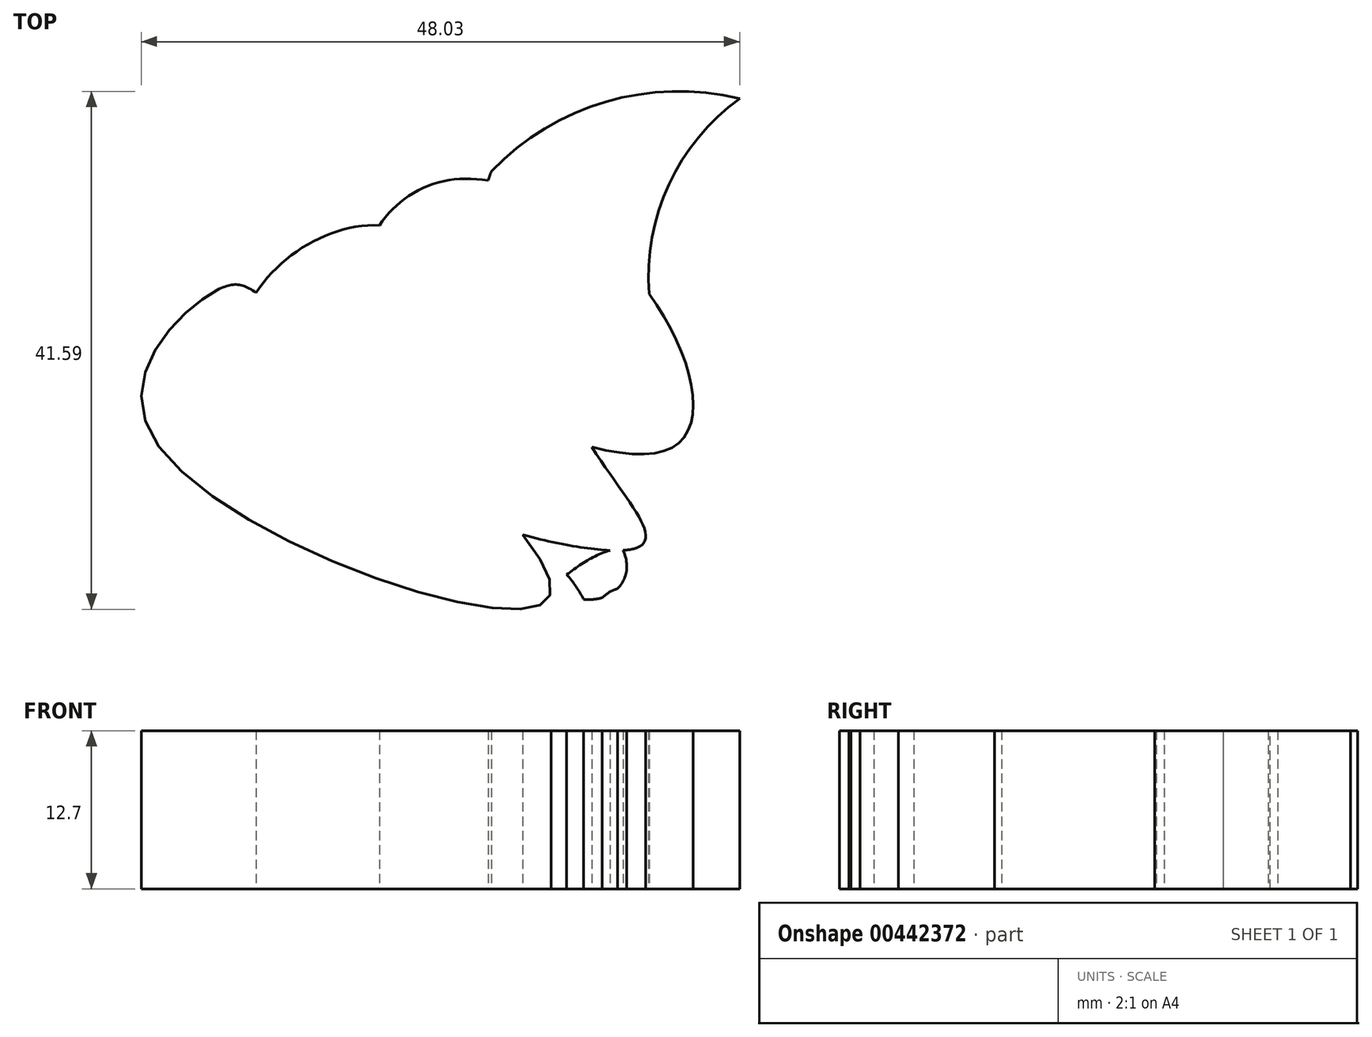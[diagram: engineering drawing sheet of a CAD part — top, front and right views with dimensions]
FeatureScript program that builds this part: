
annotation { "Feature Type Name" : "Feature", "Feature Type Description" : "" }
export const myFeature = defineFeature(function(context is Context, id is Id, definition is map)
    precondition{}
    {
        {
            var Q0;
            Q0=qCreatedBy(makeId("Top.planeOp"),FACE);
            var sketch = newSketch(context, id + "F0", { "sketchPlane" : qUnion([Q0])});
            skArc(sketch, "E0", {"start": v(-28.4, 40.22) * mm, "mid": v(-34.47, 32.4) * mm, "end": v(-35.4, 22.54) * mm});
            skArc(sketch, "E1", {"start": v(-28.4, 40.22) * mm, "mid": v(-39.13, 39.95) * mm, "end": v(-48.3, 34.38) * mm});
            skArc(sketch, "E2", {"start": v(-48.3, 34.38) * mm, "mid": v(-46, 23.94) * mm, "end": v(-35.4, 22.54) * mm});
            skSolve(sketch);
        }
        {
            var Q0;
            Q0=qCreatedBy(makeId("Top.planeOp"),FACE);
            var sketch = newSketch(context, id + "F1", { "sketchPlane" : qUnion([Q0])});
            skFitSpline(sketch, "E3", {"points": [v(-57.41, 30.02) * mm, v(-39.74, 11.43) * mm, v(-36.69, 4.11) * mm, v(-68.08, 18.14) * mm, v(-57.41, 30.02) * mm]});
            skFitSpline(sketch, "E4", {"points": [v(-43.25, 16.92) * mm, v(-36.69, 12.65) * mm, v(-36.69, 4.11) * mm, v(-43.25, 16.92) * mm]});
            skSolve(sketch);
        }
        {
            var Q0;
            Q0=qCreatedBy(makeId("Top.planeOp"),FACE);
            var sketch = newSketch(context, id + "F2", { "sketchPlane" : qUnion([Q0])});
            skPoint(sketch, "E5.3.internal.orphan", {"position": v(-41, 0) * mm});
            skFitSpline(sketch, "E6", {"points": [v(-65.13, 23.01) * mm, v(-70.3, 24.84) * mm, v(-75.8, 13.56) * mm, v(-43.8, 0) * mm, v(-65.13, 23.01) * mm]});
            skFitSpline(sketch, "E7", {"points": [v(-68.7, 19.35) * mm, v(-70.3, 24.84) * mm, v(-62.6, 24.84) * mm, v(-68.7, 19.35) * mm]});
            skSolve(sketch);
        }
        {
            var Q0;
            Q0=qCreatedBy(makeId("Top.planeOp"),FACE);
            var sketch = newSketch(context, id + "F3", { "sketchPlane" : qUnion([Q0])});
            skFitSpline(sketch, "E8", {"points": [v(-40.92, 0) * mm, v(-50.96, 9.3) * mm, v(-37.86, 4.11) * mm, v(-40.92, 0) * mm]});
            skFitSpline(sketch, "E9.trimOffspring", {"points": [v(-59.23, 0) * mm, v(-41.86, -7.47) * mm, v(-44.6, 3.81) * mm, v(-59.23, 0) * mm]});
            skPoint(sketch, "E10.0.internal.orphan", {"position": v(-57.45, 0) * mm});
            skFitSpline(sketch, "E11", {"points": [v(-41.86, -7.47) * mm, v(-34.97, -3.83) * mm, v(-38.2, 0.85) * mm, v(-41.86, -7.47) * mm]});
            skFitSpline(sketch, "E12", {"points": [v(-37.86, 4.11) * mm, v(-34.97, 0) * mm, v(-45.93, -3.83) * mm, v(-37.86, 4.11) * mm]});
            skSolve(sketch);
        }
        {
            var Q0;
            Q0=qCreatedBy(makeId("Top.planeOp"),FACE);
            var sketch = newSketch(context, id + "F4", { "sketchPlane" : qUnion([Q0])});
            skFitSpline(sketch, "E13", {"points": [v(-57.8, 24.23) * mm, v(-51.72, 33.66) * mm, v(-34.68, 23.05) * mm, v(-34.27, 11.97) * mm, v(-57.8, 24.23) * mm]});
            skSolve(sketch);
        }
        {
            var Q0;
            Q0=makeQuery(id+"F0.imprint","IMPRINT",FACE,{"disambiguationData":[TD([[makeQuery(id+"F0.imprint","IMPRINT",EDGE,{"derivedFrom":sQuery(id+"F0.wireOp",EDGE,"E0")}),-1.0]])]});
            extrude(context, id + "F5", {"entities" : qUnion([Q0]), "depth" : 12.7 * mm, "offsetDistance" : 25.4 * mm});
        }
        {
            var Q0;
            Q0=makeQuery(id+"F4.imprint","IMPRINT",FACE,{"disambiguationData":[TD([[makeQuery(id+"F4.imprint","IMPRINT",EDGE,{"derivedFrom":sQuery(id+"F4.wireOp",EDGE,"E13")}),-1.0]])]});
            var Q1;
            Q1=makeQuery(id+"F1.imprint","IMPRINT",FACE,{"disambiguationData":[TD([[makeQuery(id+"F1.imprint","IMPRINT",EDGE,{"derivedFrom":sQuery(id+"F1.wireOp",EDGE,"E3")}),-1.0]])]});
            extrude(context, id + "F6", {"entities" : qUnion([Q0, Q1]), "operationType" : NewBodyOperationType.ADD, "depth" : 12.7 * mm, "offsetDistance" : 25.4 * mm});
        }
        {
            var Q0;
            Q0=makeQuery(id+"F2.imprint","IMPRINT",FACE,{"disambiguationData":[TD([[makeQuery(id+"F2.imprint","IMPRINT",EDGE,{"derivedFrom":sQuery(id+"F2.wireOp",EDGE,"E6")}),1.0]])]});
            var Q1;
            Q1=makeQuery(id+"F3.imprint","IMPRINT",FACE,{"disambiguationData":[TD([[makeQuery(id+"F3.imprint","IMPRINT",EDGE,{"derivedFrom":sQuery(id+"F3.wireOp",EDGE,"E8")}),-1.0]])]});
            extrude(context, id + "F7", {"entities" : qUnion([Q0, Q1]), "operationType" : NewBodyOperationType.ADD, "depth" : 12.7 * mm, "offsetDistance" : 25.4 * mm});
        }
    });
